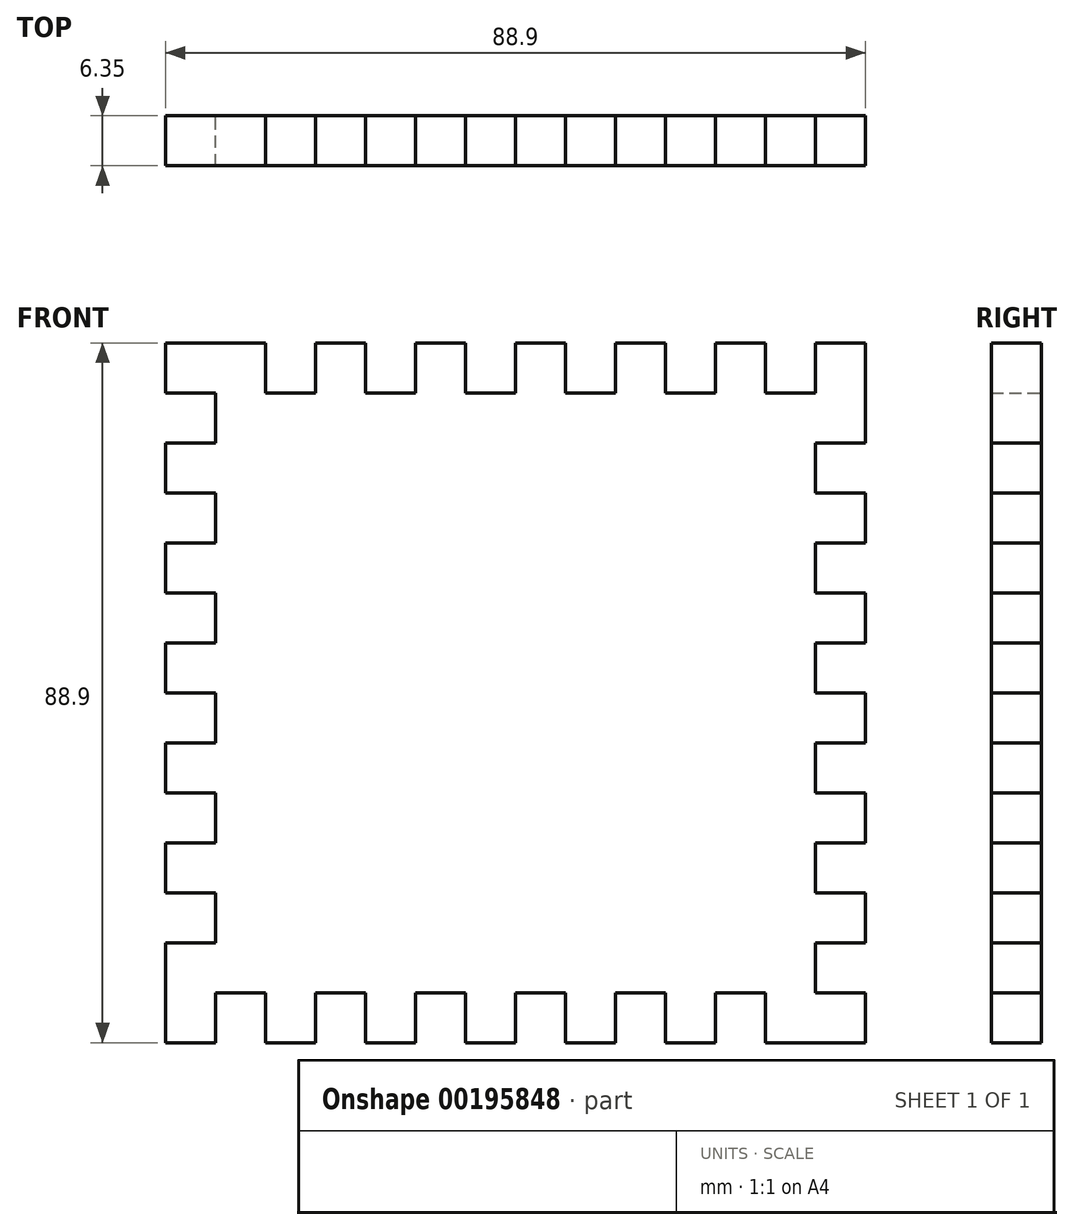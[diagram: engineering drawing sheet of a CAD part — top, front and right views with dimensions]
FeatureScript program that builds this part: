
annotation { "Feature Type Name" : "Feature", "Feature Type Description" : "" }
export const myFeature = defineFeature(function(context is Context, id is Id, definition is map)
    precondition{}
    {
        {
            var Q0;
            Q0=qCreatedBy(makeId("Front.planeOp"),FACE);
            var sketch = newSketch(context, id + "F0", { "sketchPlane" : qUnion([Q0])});
            skLineSegment(sketch, "E0.bottom", {"start": v(38.1, 38.1) * mm, "end": v(31.75, 38.1) * mm});
            skLineSegment(sketch, "E0.top", {"start": v(31.75, -38.1) * mm, "end": v(25.4, -38.1) * mm});
            skLineSegment(sketch, "E0.left", {"start": v(38.1, 31.75) * mm, "end": v(38.1, 25.4) * mm});
            skLineSegment(sketch, "E0.right", {"start": v(-38.1, 38.1) * mm, "end": v(-38.1, 31.75) * mm});
            skPoint(sketch, "E0.middle", {"position": v(0, 0) * mm});
            skLineSegment(sketch, "E1.bottom", {"start": v(44.45, 44.45) * mm, "end": v(38.1, 44.45) * mm});
            skLineSegment(sketch, "E1.top", {"start": v(44.45, -44.45) * mm, "end": v(31.75, -44.45) * mm});
            skLineSegment(sketch, "E1.left", {"start": v(44.45, 44.45) * mm, "end": v(44.45, 31.75) * mm});
            skLineSegment(sketch, "E1.right", {"start": v(-44.45, 44.45) * mm, "end": v(-44.45, 38.1) * mm});
            skLineSegment(sketch, "E2", {"start": v(-38.1, 38.1) * mm, "end": v(-44.45, 38.1) * mm});
            skLineSegment(sketch, "E3", {"start": v(-31.75, 38.1) * mm, "end": v(-31.75, 44.45) * mm});
            skLineSegment(sketch, "E4", {"start": v(-25.4, 38.1) * mm, "end": v(-25.4, 44.45) * mm});
            skLineSegment(sketch, "E5", {"start": v(-19.05, 38.1) * mm, "end": v(-19.05, 44.45) * mm});
            skLineSegment(sketch, "E6", {"start": v(-12.7, 38.1) * mm, "end": v(-12.7, 44.45) * mm});
            skLineSegment(sketch, "E7", {"start": v(-6.35, 38.1) * mm, "end": v(-6.35, 44.45) * mm});
            skLineSegment(sketch, "E8", {"start": v(0, 38.1) * mm, "end": v(0, 44.45) * mm});
            skLineSegment(sketch, "E9", {"start": v(12.7, 38.1) * mm, "end": v(12.7, 44.45) * mm});
            skLineSegment(sketch, "E10", {"start": v(19.05, 38.1) * mm, "end": v(19.05, 44.45) * mm});
            skLineSegment(sketch, "E11", {"start": v(25.4, 38.1) * mm, "end": v(25.4, 44.45) * mm});
            skLineSegment(sketch, "E12", {"start": v(31.75, 38.1) * mm, "end": v(31.75, 44.45) * mm});
            skLineSegment(sketch, "E13", {"start": v(38.1, 38.1) * mm, "end": v(38.1, 44.45) * mm});
            skLineSegment(sketch, "E14", {"start": v(6.35, 38.1) * mm, "end": v(6.35, 44.45) * mm});
            skLineSegment(sketch, "E15.trimOffspring", {"start": v(-31.75, 44.45) * mm, "end": v(-44.45, 44.45) * mm});
            skLineSegment(sketch, "E16.trimOffspring", {"start": v(-19.05, 44.45) * mm, "end": v(-25.4, 44.45) * mm});
            skLineSegment(sketch, "E17.trimOffspring", {"start": v(-6.35, 44.45) * mm, "end": v(-12.7, 44.45) * mm});
            skLineSegment(sketch, "E18.trimOffspring", {"start": v(6.35, 44.45) * mm, "end": v(0, 44.45) * mm});
            skLineSegment(sketch, "E19.trimOffspring", {"start": v(19.05, 44.45) * mm, "end": v(12.7, 44.45) * mm});
            skLineSegment(sketch, "E20.trimOffspring", {"start": v(31.75, 44.45) * mm, "end": v(25.4, 44.45) * mm});
            skLineSegment(sketch, "E21.trimOffspring", {"start": v(25.4, 38.1) * mm, "end": v(19.05, 38.1) * mm});
            skLineSegment(sketch, "E22.trimOffspring", {"start": v(12.7, 38.1) * mm, "end": v(6.35, 38.1) * mm});
            skLineSegment(sketch, "E23.trimOffspring", {"start": v(0, 38.1) * mm, "end": v(-6.35, 38.1) * mm});
            skLineSegment(sketch, "E24.trimOffspring", {"start": v(-12.7, 38.1) * mm, "end": v(-19.05, 38.1) * mm});
            skLineSegment(sketch, "E25.trimOffspring", {"start": v(-25.4, 38.1) * mm, "end": v(-31.75, 38.1) * mm});
            skLineSegment(sketch, "E26", {"start": v(38.1, 31.75) * mm, "end": v(44.45, 31.75) * mm});
            skLineSegment(sketch, "E27", {"start": v(38.1, 25.4) * mm, "end": v(44.45, 25.4) * mm});
            skLineSegment(sketch, "E28", {"start": v(38.1, 19.05) * mm, "end": v(44.45, 19.05) * mm});
            skLineSegment(sketch, "E29", {"start": v(38.1, 12.7) * mm, "end": v(44.45, 12.7) * mm});
            skLineSegment(sketch, "E30", {"start": v(38.1, 6.35) * mm, "end": v(44.45, 6.35) * mm});
            skLineSegment(sketch, "E31", {"start": v(38.1, 0) * mm, "end": v(44.45, 0) * mm});
            skLineSegment(sketch, "E32", {"start": v(38.1, -6.35) * mm, "end": v(44.45, -6.35) * mm});
            skLineSegment(sketch, "E33", {"start": v(38.1, -12.7) * mm, "end": v(44.45, -12.7) * mm});
            skLineSegment(sketch, "E34", {"start": v(38.1, -19.05) * mm, "end": v(44.45, -19.05) * mm});
            skLineSegment(sketch, "E35", {"start": v(38.1, -25.4) * mm, "end": v(44.45, -25.4) * mm});
            skLineSegment(sketch, "E36", {"start": v(38.1, -31.75) * mm, "end": v(44.45, -31.75) * mm});
            skLineSegment(sketch, "E37", {"start": v(38.1, -38.1) * mm, "end": v(44.45, -38.1) * mm});
            skLineSegment(sketch, "E38.trimOffspring", {"start": v(38.1, 19.05) * mm, "end": v(38.1, 12.7) * mm});
            skLineSegment(sketch, "E39.trimOffspring", {"start": v(38.1, 6.35) * mm, "end": v(38.1, 0) * mm});
            skLineSegment(sketch, "E40.trimOffspring", {"start": v(38.1, -6.35) * mm, "end": v(38.1, -12.7) * mm});
            skLineSegment(sketch, "E41.trimOffspring", {"start": v(38.1, -19.05) * mm, "end": v(38.1, -25.4) * mm});
            skLineSegment(sketch, "E42.trimOffspring", {"start": v(38.1, -31.75) * mm, "end": v(38.1, -38.1) * mm});
            skLineSegment(sketch, "E43.trimOffspring", {"start": v(44.45, 25.4) * mm, "end": v(44.45, 19.05) * mm});
            skLineSegment(sketch, "E44.trimOffspring", {"start": v(44.45, 12.7) * mm, "end": v(44.45, 6.35) * mm});
            skLineSegment(sketch, "E45.trimOffspring", {"start": v(44.45, 0) * mm, "end": v(44.45, -6.35) * mm});
            skLineSegment(sketch, "E46.trimOffspring", {"start": v(44.45, -12.7) * mm, "end": v(44.45, -19.05) * mm});
            skLineSegment(sketch, "E47.trimOffspring", {"start": v(44.45, -25.4) * mm, "end": v(44.45, -31.75) * mm});
            skLineSegment(sketch, "E48.trimOffspring", {"start": v(44.45, -38.1) * mm, "end": v(44.45, -44.45) * mm});
            skLineSegment(sketch, "E49", {"start": v(31.75, -38.1) * mm, "end": v(31.75, -44.45) * mm});
            skLineSegment(sketch, "E50", {"start": v(25.4, -38.1) * mm, "end": v(25.4, -44.45) * mm});
            skLineSegment(sketch, "E51", {"start": v(19.05, -38.1) * mm, "end": v(19.05, -44.45) * mm});
            skLineSegment(sketch, "E52", {"start": v(12.7, -38.1) * mm, "end": v(12.7, -44.45) * mm});
            skLineSegment(sketch, "E53", {"start": v(6.35, -38.1) * mm, "end": v(6.35, -44.45) * mm});
            skLineSegment(sketch, "E54", {"start": v(0, -38.1) * mm, "end": v(0, -44.45) * mm});
            skLineSegment(sketch, "E55", {"start": v(-6.35, -38.1) * mm, "end": v(-6.35, -44.45) * mm});
            skLineSegment(sketch, "E56", {"start": v(-12.7, -38.1) * mm, "end": v(-12.7, -44.45) * mm});
            skLineSegment(sketch, "E57", {"start": v(-19.05, -38.1) * mm, "end": v(-19.05, -44.45) * mm});
            skLineSegment(sketch, "E58", {"start": v(-25.4, -38.1) * mm, "end": v(-25.4, -44.45) * mm});
            skLineSegment(sketch, "E59", {"start": v(-31.75, -38.1) * mm, "end": v(-31.75, -44.45) * mm});
            skLineSegment(sketch, "E60", {"start": v(-38.1, -38.1) * mm, "end": v(-38.1, -44.45) * mm});
            skLineSegment(sketch, "E61.trimOffspring", {"start": v(25.4, -44.45) * mm, "end": v(19.05, -44.45) * mm});
            skLineSegment(sketch, "E62.trimOffspring", {"start": v(12.7, -44.45) * mm, "end": v(6.35, -44.45) * mm});
            skLineSegment(sketch, "E63.trimOffspring", {"start": v(0, -44.45) * mm, "end": v(-6.35, -44.45) * mm});
            skLineSegment(sketch, "E64.trimOffspring", {"start": v(-12.7, -44.45) * mm, "end": v(-19.05, -44.45) * mm});
            skLineSegment(sketch, "E65.trimOffspring", {"start": v(-25.4, -44.45) * mm, "end": v(-31.75, -44.45) * mm});
            skLineSegment(sketch, "E66", {"start": v(-31.75, -44.45) * mm, "end": v(-31.75, -44.45) * mm});
            skLineSegment(sketch, "E67", {"start": v(-38.1, -44.45) * mm, "end": v(-44.45, -44.45) * mm});
            skLineSegment(sketch, "E68.trimOffspring", {"start": v(-31.75, -38.1) * mm, "end": v(-38.1, -38.1) * mm});
            skLineSegment(sketch, "E69.trimOffspring", {"start": v(-19.05, -38.1) * mm, "end": v(-25.4, -38.1) * mm});
            skLineSegment(sketch, "E70.trimOffspring", {"start": v(-6.35, -38.1) * mm, "end": v(-12.7, -38.1) * mm});
            skLineSegment(sketch, "E71.trimOffspring", {"start": v(6.35, -38.1) * mm, "end": v(0, -38.1) * mm});
            skLineSegment(sketch, "E72.trimOffspring", {"start": v(19.05, -38.1) * mm, "end": v(12.7, -38.1) * mm});
            skLineSegment(sketch, "E73", {"start": v(-44.45, -31.75) * mm, "end": v(-38.1, -31.75) * mm});
            skLineSegment(sketch, "E74", {"start": v(-44.45, -25.4) * mm, "end": v(-38.1, -25.4) * mm});
            skLineSegment(sketch, "E75", {"start": v(-44.45, -19.05) * mm, "end": v(-38.1, -19.05) * mm});
            skLineSegment(sketch, "E76", {"start": v(-44.45, -12.7) * mm, "end": v(-38.1, -12.7) * mm});
            skLineSegment(sketch, "E77", {"start": v(-44.45, -6.35) * mm, "end": v(-38.1, -6.35) * mm});
            skLineSegment(sketch, "E78", {"start": v(-44.45, 0) * mm, "end": v(-38.1, 0) * mm});
            skLineSegment(sketch, "E79", {"start": v(-44.45, 6.35) * mm, "end": v(-38.1, 6.35) * mm});
            skLineSegment(sketch, "E80", {"start": v(-44.45, 12.7) * mm, "end": v(-38.1, 12.7) * mm});
            skLineSegment(sketch, "E81", {"start": v(-44.45, 19.05) * mm, "end": v(-38.1, 19.05) * mm});
            skLineSegment(sketch, "E82", {"start": v(-44.45, 25.4) * mm, "end": v(-38.1, 25.4) * mm});
            skLineSegment(sketch, "E83", {"start": v(-44.45, 31.75) * mm, "end": v(-38.1, 31.75) * mm});
            skLineSegment(sketch, "E84.trimOffspring", {"start": v(-44.45, -31.75) * mm, "end": v(-44.45, -44.45) * mm});
            skLineSegment(sketch, "E85.trimOffspring", {"start": v(-44.45, -19.05) * mm, "end": v(-44.45, -25.4) * mm});
            skLineSegment(sketch, "E86.trimOffspring", {"start": v(-44.45, -6.35) * mm, "end": v(-44.45, -12.7) * mm});
            skLineSegment(sketch, "E87.trimOffspring", {"start": v(-44.45, 6.35) * mm, "end": v(-44.45, 0) * mm});
            skLineSegment(sketch, "E88.trimOffspring", {"start": v(-44.45, 19.05) * mm, "end": v(-44.45, 12.7) * mm});
            skLineSegment(sketch, "E89.trimOffspring", {"start": v(-44.45, 31.75) * mm, "end": v(-44.45, 25.4) * mm});
            skLineSegment(sketch, "E90.trimOffspring", {"start": v(-38.1, 25.4) * mm, "end": v(-38.1, 19.05) * mm});
            skLineSegment(sketch, "E91.trimOffspring", {"start": v(-38.1, 12.7) * mm, "end": v(-38.1, 6.35) * mm});
            skLineSegment(sketch, "E92.trimOffspring", {"start": v(-38.1, 0) * mm, "end": v(-38.1, -6.35) * mm});
            skLineSegment(sketch, "E93.trimOffspring", {"start": v(-38.1, -12.7) * mm, "end": v(-38.1, -19.05) * mm});
            skLineSegment(sketch, "E94.trimOffspring", {"start": v(-38.1, -25.4) * mm, "end": v(-38.1, -31.75) * mm});
            skSolve(sketch);
        }
        {
            var Q0;
            Q0 = qSketchRegion(id + "F0", true);
            extrude(context, id + "F1", {"entities" : qUnion([Q0]), "depth" : 6.35 * mm});
        }
    });
